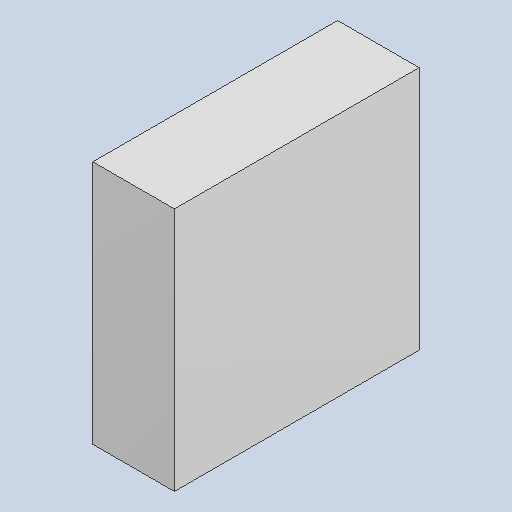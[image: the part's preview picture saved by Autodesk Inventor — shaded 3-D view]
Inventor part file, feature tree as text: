
AUTODESK INVENTOR PART (.ipt)
format: ipt  version: 2023.4 (Build 274418000, 418)  size: 81,408 bytes
history: native  units: mm
features: extrude x1
ambient origin geometry x8: Origin, YZ Plane, XZ Plane, XY Plane, X Axis, Y Axis, Z Axis, Center Point
bodies: Solid1 (feature_tree)
feature tree (1):
  extrude  "Extruded_43"  [1 undecoded]
note: 1 required parameter value undecoded (feature->parameter linkage not recoverable at this tier; creation-order binding heuristic only, values carry confidence <= 0.55)
